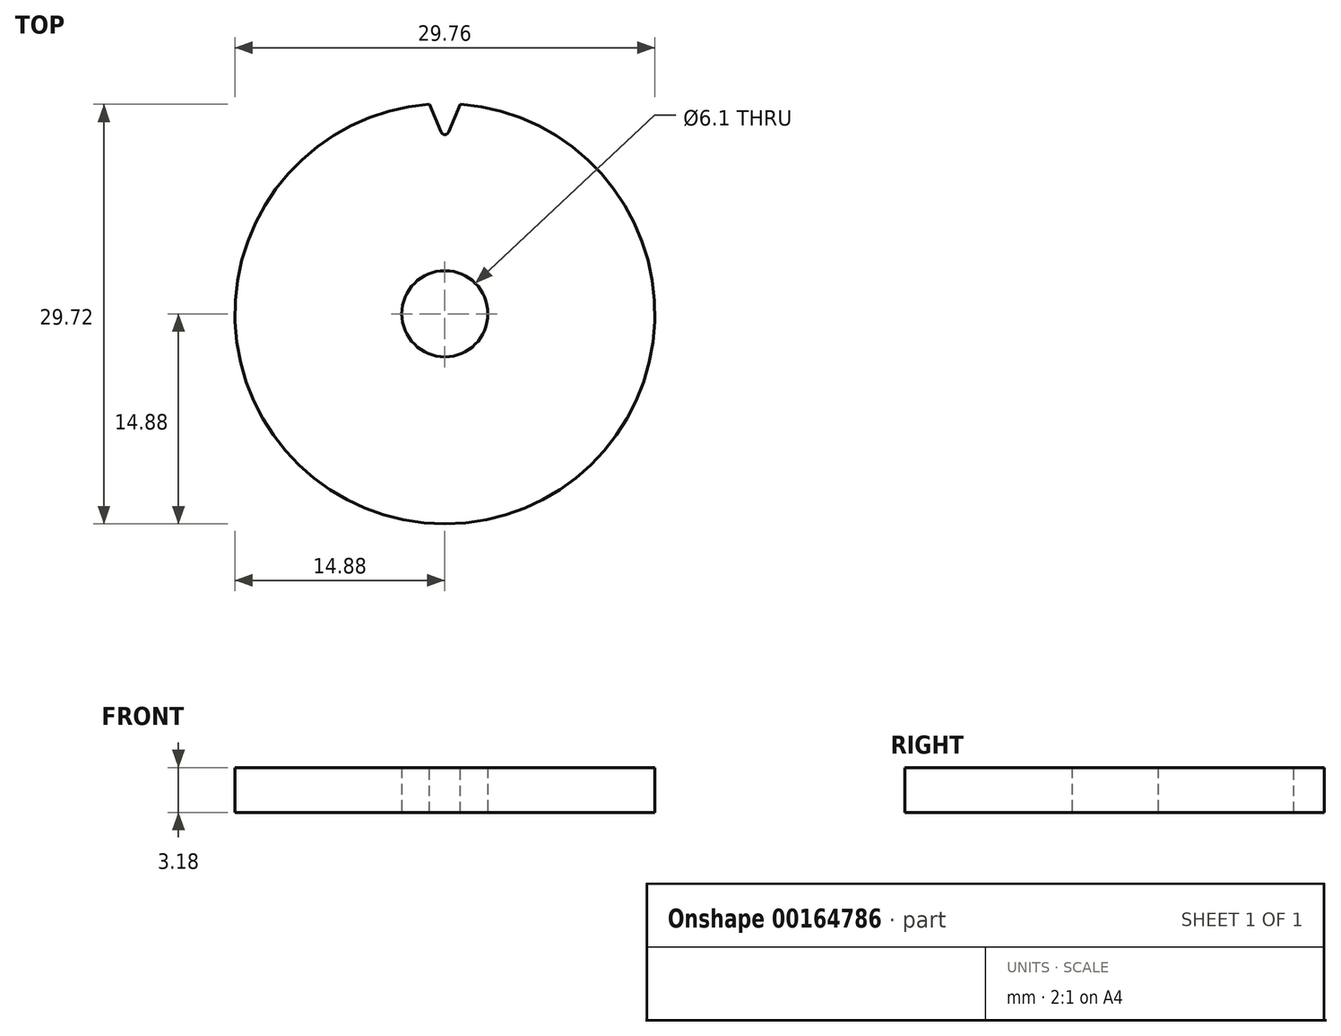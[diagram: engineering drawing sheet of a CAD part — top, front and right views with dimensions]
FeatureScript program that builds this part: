
annotation { "Feature Type Name" : "Feature", "Feature Type Description" : "" }
export const myFeature = defineFeature(function(context is Context, id is Id, definition is map)
    precondition{}
    {
        {
            var Q0;
            Q0=qCreatedBy(makeId("Top.planeOp"),FACE);
            var sketch = newSketch(context, id + "F0", { "sketchPlane" : qUnion([Q0])});
            skCircle(sketch, "E0", {"center": v(0, 0) * mm, "radius": 14.88 * mm});
            skCircle(sketch, "E1", {"center": v(0, 0) * mm, "radius": 3.05 * mm});
            skSolve(sketch);
        }
        {
            var Q0;
            Q0=qSketchRegion(id+"F0",true);
            extrude(context, id + "F1", {"entities" : qUnion([Q0]), "depth" : 3.17 * mm});
        }
        {
            var Q0;
            Q0=makeQuery(id+"F1.opExtrude","CAP_FACE",FACE,{"disambiguationData":[OSD([sQuery(id+"F0.wireOp",EDGE,"E0"),sQuery(id+"F0.wireOp",EDGE,"kzjH0w8L-SzTJ-EdVv-AyzX-BKC8k2flX5Ux"),sQuery(id+"F0.wireOp",EDGE,"cB56IUw9-Wqvp-4MSO-hsBC-B7dZXn05IXyB"),sQuery(id+"F0.wireOp",EDGE,"hefJExKC-cNzo-r410-gYXa-Mdlhh4D0BsHS"),sQuery(id+"F0.wireOp",EDGE,"55zMJ0u0-ymDK-EYCK-2BBR-O91F1kH4I6Zc")])],"isStart":false});
            var sketch = newSketch(context, id + "F2", { "sketchPlane" : qUnion([Q0])});
            skLineSegment(sketch, "E2", {"start": v(0, 0) * mm, "end": v(0, 14.88) * mm, "construction": true});
            skArc(sketch, "E3", {"start": v(1.1, 14.84) * mm, "mid": v(0, 14.88) * mm, "end": v(-1.1, 14.84) * mm});
            skLineSegment(sketch, "E4", {"start": v(-1.1, 14.84) * mm, "end": v(-0.27, 12.87) * mm});
            skLineSegment(sketch, "E5", {"start": v(1.1, 14.84) * mm, "end": v(0.27, 12.87) * mm});
            skArc(sketch, "E6", {"start": v(-0.27, 12.87) * mm, "mid": v(0, 12.69) * mm, "end": v(0.27, 12.87) * mm});
            skLineSegment(sketch, "E7", {"start": v(0, 0) * mm, "end": v(0.74, 14.86) * mm, "construction": true});
            skPoint(sketch, "E8", {"position": v(0.69, 13.85) * mm});
            skSolve(sketch);
        }
        {
            var Q0;
            Q0=qSketchRegion(id+"F2",true);
            var Q1;
            Q1=makeQuery(id+"F1.opExtrude","CAP_FACE",FACE,{"disambiguationData":[OSD([sQuery(id+"F0.wireOp",EDGE,"E0"),sQuery(id+"F0.wireOp",EDGE,"kzjH0w8L-SzTJ-EdVv-AyzX-BKC8k2flX5Ux"),sQuery(id+"F0.wireOp",EDGE,"cB56IUw9-Wqvp-4MSO-hsBC-B7dZXn05IXyB"),sQuery(id+"F0.wireOp",EDGE,"hefJExKC-cNzo-r410-gYXa-Mdlhh4D0BsHS"),sQuery(id+"F0.wireOp",EDGE,"55zMJ0u0-ymDK-EYCK-2BBR-O91F1kH4I6Zc")])],"isStart":true});
            extrude(context, id + "F3", {"entities" : qUnion([Q0]), "operationType" : NewBodyOperationType.REMOVE, "endBound" : BoundingType.UP_TO_SURFACE, "oppositeDirection" : true, "endBoundEntityFace" : qUnion([Q1]), "depth" : 25.4 * mm});
        }
    });
